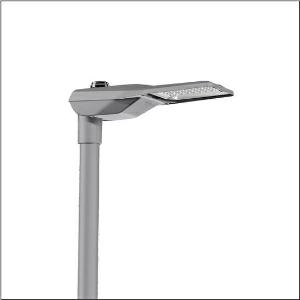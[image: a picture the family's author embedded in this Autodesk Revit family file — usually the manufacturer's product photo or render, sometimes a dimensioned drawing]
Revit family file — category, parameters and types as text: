
# Revit family: streetlight_sl_21_mini___pl52_5xe6h37n08gb_6e65
name_source: partatom
category: Lighting Fixtures
units: mm (PartAtom-declared; Revit-internal decimal feet)

## family parameters
Cut with Voids When Loaded = No
Host = Face
Light Source = No
Part Type = Normal
Room Calculation Point = No
Round Connector Dimension = Use Diameter
Shared = No

## types (1)
- --- (1 x LED, 5840 lm, 40.4 W, 3000K)
    Apparent Load = 40 VA
    CIE Flux Codes = 27 59 98 100 100
    Color Rendering = 70
    Color Temperature = 3000K
    Default Elevation = 1800 mm
    Description = Streetlight SL 21 mini, mast luminaire, primary light control with lens, of PMMA, primary optical cover: cover, of toughened safety glass, transparent, light distribution: PL52, light emission: direct distribution, primary light characteristic: asymmetric, installation type: side-entry, LED, 3G 1.5mm², High Power LED, rated luminous flux: 5.840lm, luminous efficacy: 145lm/W, light colour: 730, colour temperature: 3000K, control gear: NEMA (7pin), control: overheat protection, pre-setting: linear dimming characteristic, constant luminous flux control, time-dependent luminous flux control, flexible luminous flux parameterisation, mains connection: 230..240V, AC, 50/60Hz, connection cable pre-assembled, cable length: 8,5m, wiring characteristics: H07RN-F, start of lifetime: 40W, end of service life: 41W, reduction: 19W, luminaire housing, of diecast aluminium (EN AC-44300), powder-coated, Siteco® metallic grey (DB 702S), corrosivity category C5 high according to DIN EN ISO 12944, multi-level sealing system, sealing non-destructively replaceable, inclination adjustable: 0°, 5°, 10°, 15°, length: 628mm, width: 235mm, height: 110mm, spigot size: 42mm (side-entry), mounting height: 4..8m, protection rating (complete): IP66, insulation class (complete): insulation class I (protective earthing), certification: CE, ENEC, ENEC+, VDE, impact resistance: IK10, permissible operating ambient temperature for outdoor applications: -40..+50°C, standard-compliant lighting for roads and squares, packaging unit: 1 piece

Light Distribution: PL52
    Height = 110 mm
    Lamp = 1 x LED
    Lamp Light Flux = 5840 lm
    Lamp Power = 40.4 W
    Lamp count = 1
    Length = 625 mm
    Luminous efficacy = 145 lm/W
    Manufacturer = Siteco
    ModVariant = No
    Model = 5XE6H37N08GB
    Number of Poles = 1
    OnlyDefault = Yes
    Power Factor = 1
    Product Name = Streetlight SL 21 mini | PL52
    Product group = mast luminaire | pylon top
    ProductGroupID = 6100
    Protection Class = Protection class I
    Protection Degree = IP 66
    RLX_Detail_Level = 1
    RLX_Emergency_Light_Flux = 0 lm
    RLX_Emergency_Type = 0
    RLX_Emergency_Type_DB = No
    RlxData = <blob elided: 35429 chars, md5=d46a8a92>
    Socket = socket
    Standby Power = 0 W
    System Light Flux = 5840 lm
    System Power = 40 W
    Type Comments = factory setting: luminous flux: 100 % | dim-lin: 254 | 812 mA
    Type Image = l_1294379.jpg
    URL = http://relux.com
    VarID = @adj_140361
    Voltage = 0 V
    Weight = 0.00 kg
    Width = 234 mm

## geometry (parser evidence)
native form markers: Blend x4, Sweep x12
no freeform markers — native parametric forms only
